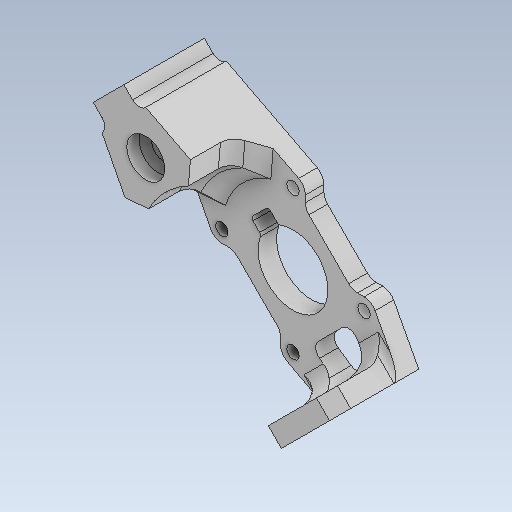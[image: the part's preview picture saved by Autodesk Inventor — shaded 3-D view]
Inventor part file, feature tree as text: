
AUTODESK INVENTOR PART (.ipt)
format: ipt  version: 2020 (Build 240168000, 168)  size: 343,040 bytes
history: native  units: mm
features: sketch x9, other x3, plane x2
ambient origin geometry x8: Origin, YZ Plane, XZ Plane, XY Plane, X Axis, Y Axis, Z Axis, Center Point
bodies: Solid1 (feature_tree)
feature tree (14):
  other  "mot_holder_1.ipt"
  other  "Solid1::mot_holder_1.ipt"
  other  "TaggingFeature1"
  sketch  "Sketch1"  dims[d0=10.0mm]
  sketch  "Sketch2"
  sketch  "Sketch3"
  sketch  "Sketch4"
  sketch  "Sketch10"
  sketch  "Sketch11"
  sketch  "Sketch12"
  sketch  "Sketch13"
  sketch  "Sketch14"
  plane  "Work Plane1"
  plane  "Work Plane2"
